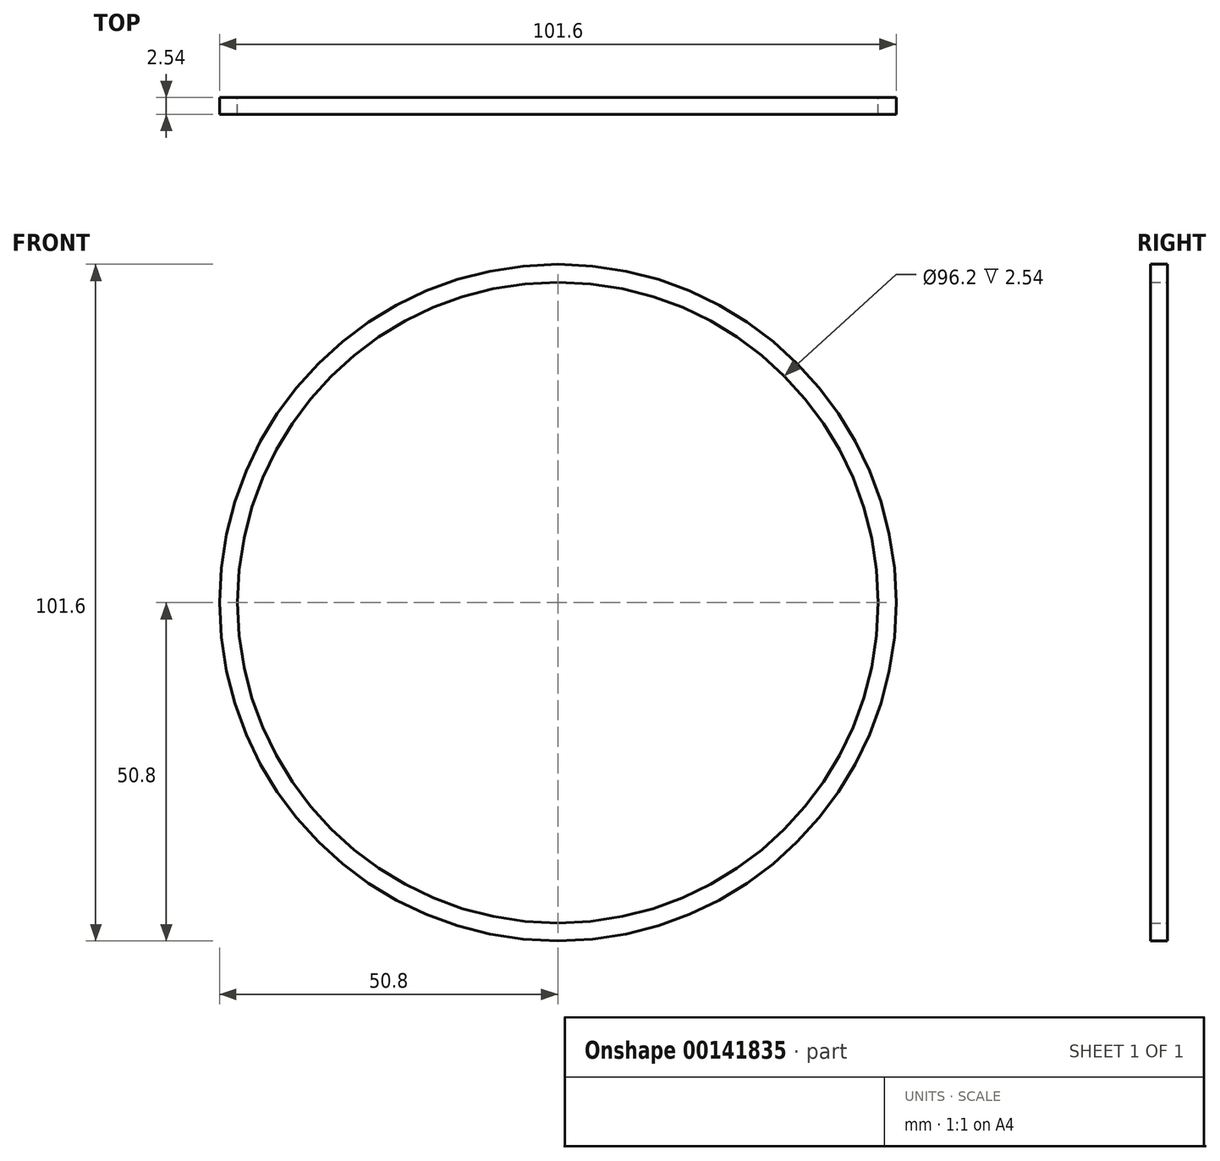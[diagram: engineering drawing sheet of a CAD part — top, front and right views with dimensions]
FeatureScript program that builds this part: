
annotation { "Feature Type Name" : "Feature", "Feature Type Description" : "" }
export const myFeature = defineFeature(function(context is Context, id is Id, definition is map)
    precondition{}
    {
        {
            var Q0;
            Q0=qCreatedBy(makeId("Front.planeOp"),FACE);
            var sketch = newSketch(context, id + "F0", { "sketchPlane" : qUnion([Q0])});
            skCircle(sketch, "E0", {"center": v(0, 0) * mm, "radius": 50.8 * mm});
            skCircle(sketch, "E1", {"center": v(0, 0) * mm, "radius": 48.1 * mm});
            skSolve(sketch);
        }
        {
            var Q0;
            Q0=makeQuery(id+"F0.imprint","IMPRINT",FACE,{"disambiguationData":[TD([[makeQuery(id+"F0.imprint","IMPRINT",EDGE,{"derivedFrom":sQuery(id+"F0.wireOp",EDGE,"E0")}),1.0]])]});
            extrude(context, id + "F1", {"entities" : qUnion([Q0]), "depth" : 2.54 * mm});
        }
    });
